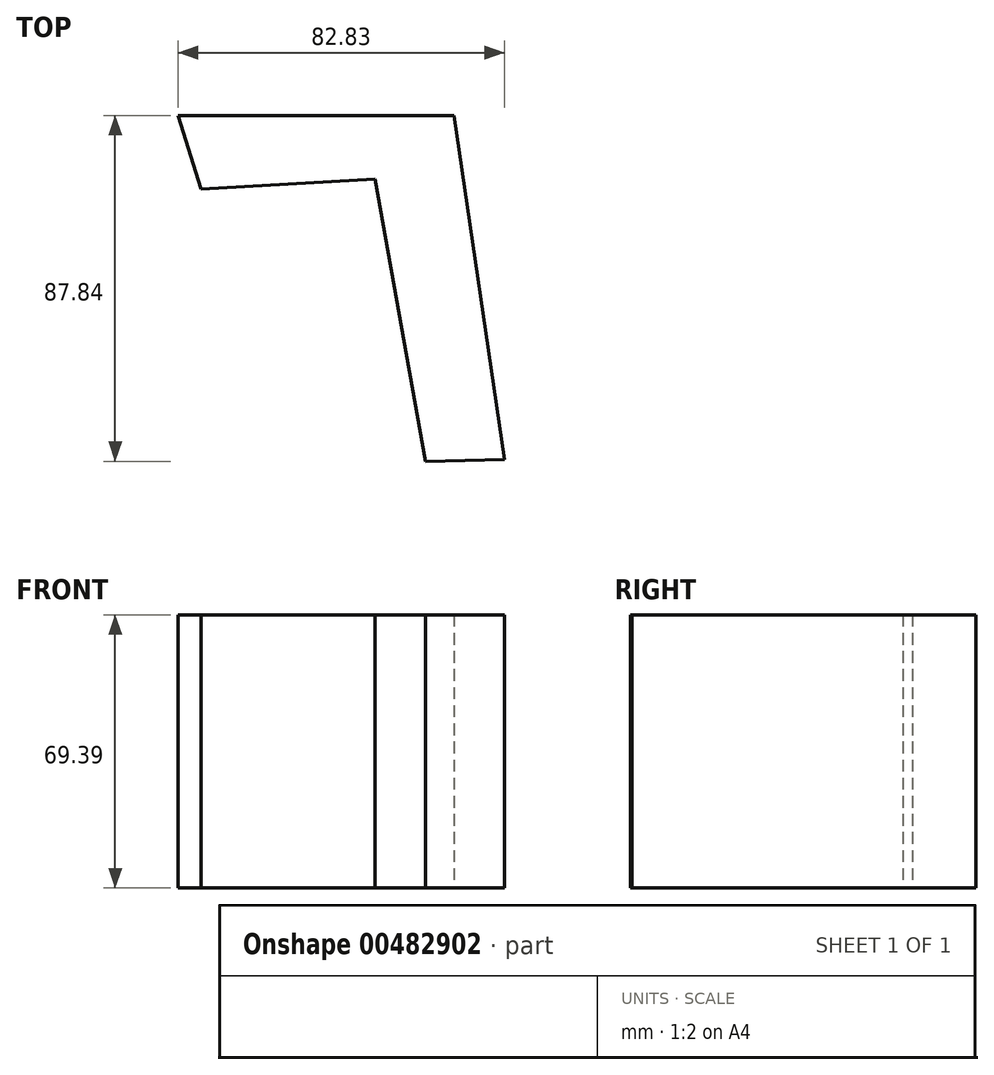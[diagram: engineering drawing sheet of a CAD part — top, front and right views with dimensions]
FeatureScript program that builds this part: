
annotation { "Feature Type Name" : "Feature", "Feature Type Description" : "" }
export const myFeature = defineFeature(function(context is Context, id is Id, definition is map)
    precondition{}
    {
        {
            var Q0;
            Q0=qCreatedBy(makeId("Top.planeOp"),FACE);
            var sketch = newSketch(context, id + "F0", { "sketchPlane" : qUnion([Q0])});
            skLineSegment(sketch, "E0", {"start": v(-54.8, 42.6) * mm, "end": v(15.21, 42.6) * mm});
            skLineSegment(sketch, "E1", {"start": v(15.21, 42.6) * mm, "end": v(28.03, -44.76) * mm});
            skLineSegment(sketch, "E2", {"start": v(28.03, -44.76) * mm, "end": v(7.97, -45.25) * mm});
            skLineSegment(sketch, "E3", {"start": v(7.97, -45.25) * mm, "end": v(-4.85, 26.41) * mm});
            skLineSegment(sketch, "E4", {"start": v(-4.85, 26.41) * mm, "end": v(-49.01, 23.98) * mm});
            skLineSegment(sketch, "E5", {"start": v(-54.8, 42.6) * mm, "end": v(-49.01, 23.98) * mm});
            skSolve(sketch);
        }
        {
            var Q0;
            Q0=makeQuery(id+"F0.imprint","IMPRINT",FACE,{"disambiguationData":[TD([[makeQuery(id+"F0.imprint","IMPRINT",EDGE,{"derivedFrom":sQuery(id+"F0.wireOp",EDGE,"E0")}),-1.0]])]});
            extrude(context, id + "F1", {"entities" : qUnion([Q0]), "depth" : 69.39 * mm});
        }
    });
